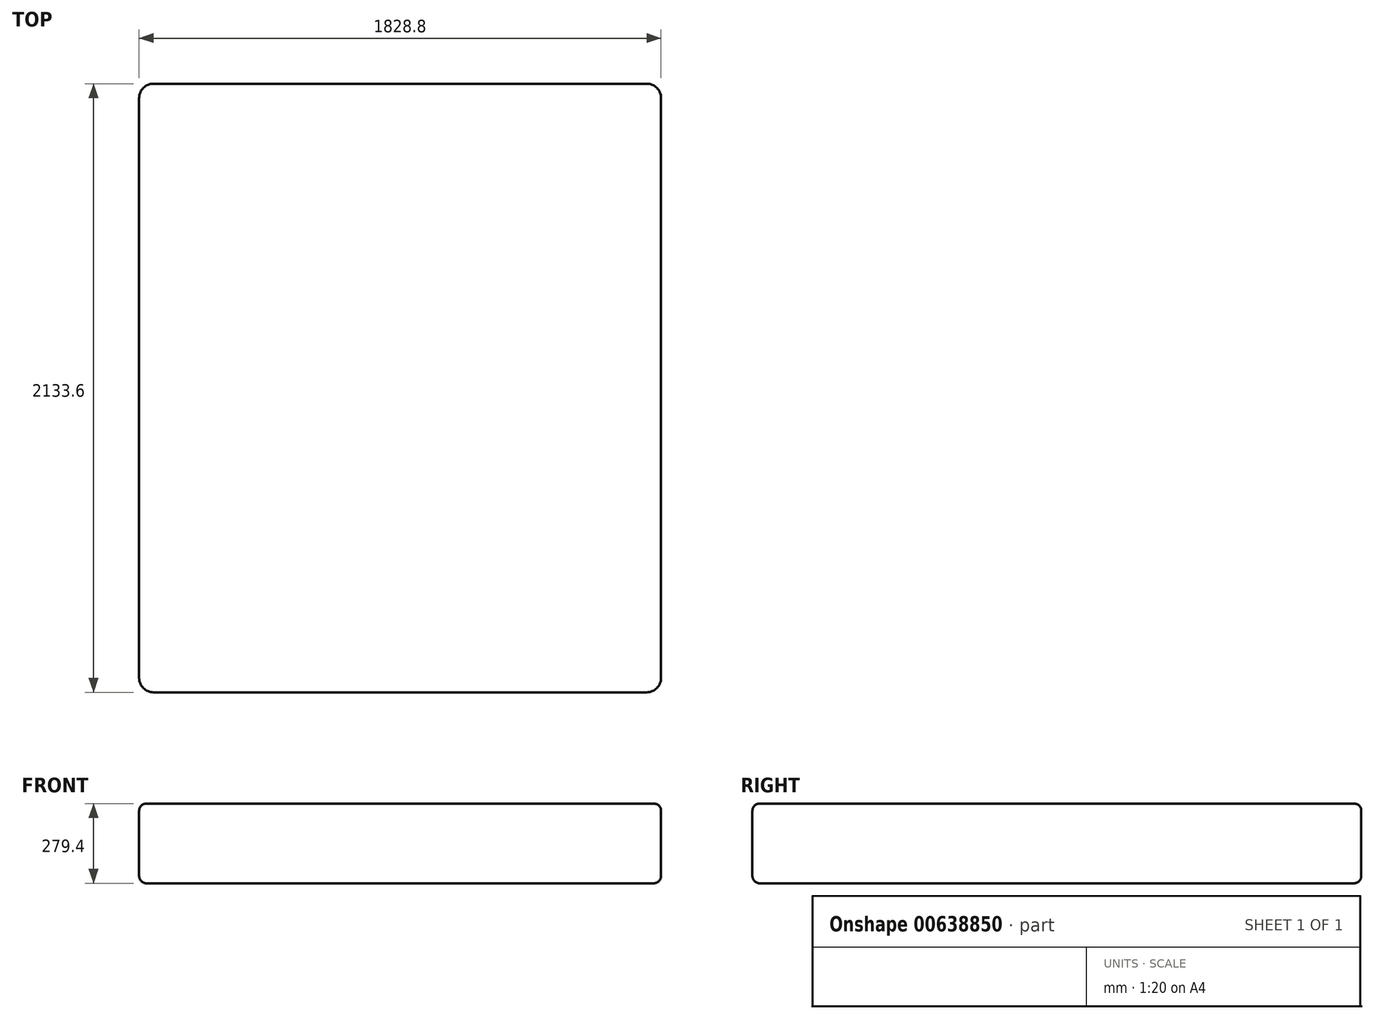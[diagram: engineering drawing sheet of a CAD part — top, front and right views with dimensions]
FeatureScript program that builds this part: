
annotation { "Feature Type Name" : "Feature", "Feature Type Description" : "" }
export const myFeature = defineFeature(function(context is Context, id is Id, definition is map)
    precondition{}
    {
        {
            var Q0;
            Q0=qCreatedBy(makeId("Top.planeOp"),FACE);
            var sketch = newSketch(context, id + "F0", { "sketchPlane" : qUnion([Q0])});
            skLineSegment(sketch, "E0.bottom", {"start": v(914.4, 1066.8) * mm, "end": v(-914.4, 1066.8) * mm});
            skLineSegment(sketch, "E0.top", {"start": v(914.4, -1066.8) * mm, "end": v(-914.4, -1066.8) * mm});
            skLineSegment(sketch, "E0.left", {"start": v(914.4, 1066.8) * mm, "end": v(914.4, -1066.8) * mm});
            skLineSegment(sketch, "E0.right", {"start": v(-914.4, 1066.8) * mm, "end": v(-914.4, -1066.8) * mm});
            skPoint(sketch, "E0.middle", {"position": v(0, 0) * mm});
            skSolve(sketch);
        }
        {
            var Q0;
            Q0=makeQuery(id+"F0.imprint","IMPRINT",FACE,{"disambiguationData":[TD([[makeQuery(id+"F0.imprint","IMPRINT",EDGE,{"derivedFrom":sQuery(id+"F0.wireOp",EDGE,"E0.bottom")}),1.0]])]});
            extrude(context, id + "F1", {"entities" : qUnion([Q0]), "depth" : 279.4 * mm, "offsetDistance" : 25.4 * mm});
        }
        {
            var Q0;
            Q0=makeQuery(id+"F1.opExtrude","SWEPT_EDGE",EDGE,{"disambiguationData":[OSD([sQuery(id+"F0.wireOp",EDGE,"E0.top"),sQuery(id+"F0.wireOp",EDGE,"E0.right")])]});
            var Q1;
            Q1=makeQuery(id+"F1.opExtrude","SWEPT_EDGE",EDGE,{"disambiguationData":[OSD([sQuery(id+"F0.wireOp",EDGE,"E0.bottom"),sQuery(id+"F0.wireOp",EDGE,"E0.right")])]});
            var Q2;
            Q2=makeQuery(id+"F1.opExtrude","SWEPT_EDGE",EDGE,{"disambiguationData":[OSD([sQuery(id+"F0.wireOp",EDGE,"E0.top"),sQuery(id+"F0.wireOp",EDGE,"E0.left")])]});
            var Q3;
            Q3=makeQuery(id+"F1.opExtrude","SWEPT_EDGE",EDGE,{"disambiguationData":[OSD([sQuery(id+"F0.wireOp",EDGE,"E0.bottom"),sQuery(id+"F0.wireOp",EDGE,"E0.left")])]});
            fillet(context, id + "F2", {"entities" : qUnion([Q0, Q1, Q2, Q3]), "radius" : 50.8 * mm, "tangentPropagation" : true, "allowEdgeOverflow" : false});
        }
        {
            var Q0;
            Q0=makeQuery(id+"F1.opExtrude","CAP_EDGE",EDGE,{"disambiguationData":[OSD([sQuery(id+"F0.wireOp",EDGE,"E0.top")])],"isStart":false});
            var Q1;
            {var subQ0=sQuery(id+"F0.wireOp",EDGE,"E0.left");var subQ1=sQuery(id+"F0.wireOp",EDGE,"E0.top");Q1=makeQuery(id+"F2.opFillet","BLEND_EDGE",EDGE,{"blendedFrom":[makeQuery(id+"F1.opExtrude","SWEPT_EDGE",EDGE,{"disambiguationData":[OSD([subQ1,subQ0])]}),makeQuery(id+"F1.opExtrude","CAP_FACE",FACE,{"disambiguationData":[OSD([sQuery(id+"F0.wireOp",EDGE,"E0.bottom"),subQ1,subQ0,sQuery(id+"F0.wireOp",EDGE,"E0.right")])],"isStart":false})],"blendedInto":[makeQuery(id+"F1.opExtrude","CAP_FACE",FACE,{"disambiguationData":[OSD([sQuery(id+"F0.wireOp",EDGE,"E0.bottom"),subQ1,subQ0,sQuery(id+"F0.wireOp",EDGE,"E0.right")])],"isStart":false})]});}
            var Q2;
            Q2=makeQuery(id+"F1.opExtrude","CAP_EDGE",EDGE,{"disambiguationData":[OSD([sQuery(id+"F0.wireOp",EDGE,"E0.left")])],"isStart":false});
            var Q3;
            Q3=makeQuery(id+"F1.opExtrude","CAP_EDGE",EDGE,{"disambiguationData":[OSD([sQuery(id+"F0.wireOp",EDGE,"E0.top")])],"isStart":true});
            fillet(context, id + "F3", {"entities" : qUnion([Q0, Q1, Q2, Q3]), "radius" : 25.4 * mm, "tangentPropagation" : true, "allowEdgeOverflow" : false});
        }
    });
